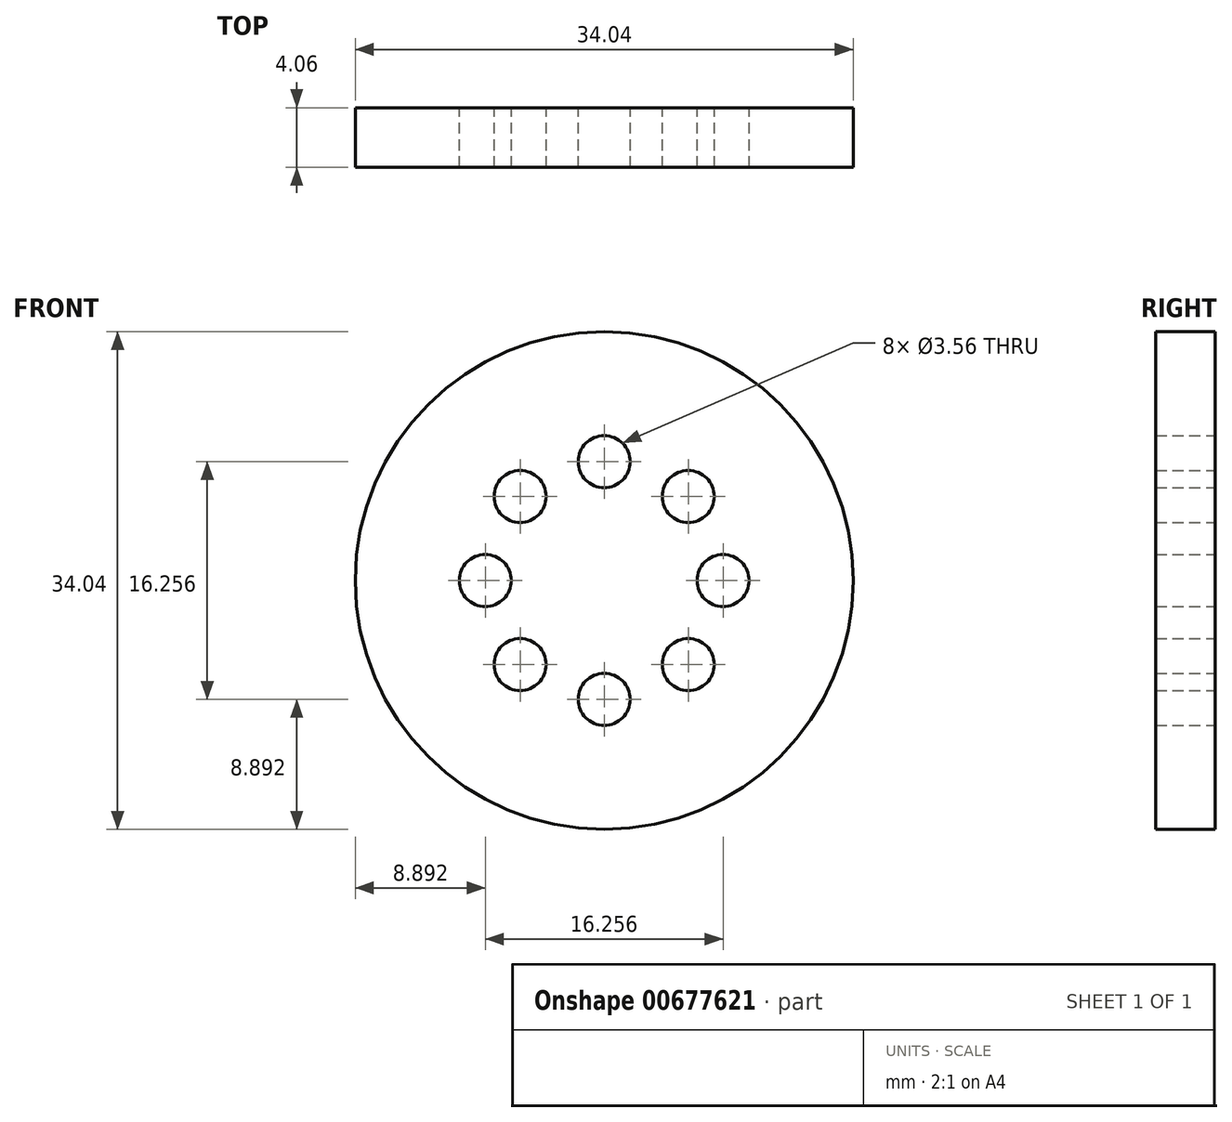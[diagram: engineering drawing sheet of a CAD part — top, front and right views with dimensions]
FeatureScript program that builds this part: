
annotation { "Feature Type Name" : "Feature", "Feature Type Description" : "" }
export const myFeature = defineFeature(function(context is Context, id is Id, definition is map)
    precondition{}
    {
        {
            var Q0;
            Q0=qCreatedBy(makeId("Front.planeOp"),FACE);
            var sketch = newSketch(context, id + "F0", { "sketchPlane" : qUnion([Q0])});
            skCircle(sketch, "E0", {"center": v(0, 0) * mm, "radius": 17.02 * mm});
            skSolve(sketch);
        }
        {
            var Q0;
            Q0=makeQuery(id+"F0.imprint","IMPRINT",FACE,{"disambiguationData":[TD([[makeQuery(id+"F0.imprint","IMPRINT",EDGE,{"derivedFrom":sQuery(id+"F0.wireOp",EDGE,"E0")}),1.0]])]});
            var sketch = newSketch(context, id + "F1", { "sketchPlane" : qUnion([Q0])});
            skCircle(sketch, "E1", {"center": v(0, -8.13) * mm, "radius": 1.78 * mm});
            skCircle(sketch, "E2.1.0", {"center": v(5.75, -5.75) * mm, "radius": 1.78 * mm});
            skCircle(sketch, "E2.2.0", {"center": v(8.13, 0) * mm, "radius": 1.78 * mm});
            skCircle(sketch, "E2.3.0", {"center": v(5.75, 5.75) * mm, "radius": 1.78 * mm});
            skCircle(sketch, "E2.4.0", {"center": v(0, 8.13) * mm, "radius": 1.78 * mm});
            skCircle(sketch, "E2.5.0", {"center": v(-5.75, 5.75) * mm, "radius": 1.78 * mm});
            skCircle(sketch, "E2.6.0", {"center": v(-8.13, 0) * mm, "radius": 1.78 * mm});
            skCircle(sketch, "E2.7.0", {"center": v(-5.75, -5.75) * mm, "radius": 1.78 * mm});
            skPoint(sketch, "E2.center", {"position": v(0, 0) * mm});
            skSolve(sketch);
        }
        {
            var Q0;
            Q0=makeQuery(id+"F0.imprint","IMPRINT",FACE,{"disambiguationData":[TD([[makeQuery(id+"F0.imprint","IMPRINT",EDGE,{"derivedFrom":sQuery(id+"F0.wireOp",EDGE,"E0")}),1.0]])]});
            extrude(context, id + "F2", {"entities" : qUnion([Q0]), "depth" : 4.06 * mm, "offsetDistance" : 25.4 * mm});
        }
        {
            var Q0;
            Q0=makeQuery(id+"F1.imprint","IMPRINT",FACE,{"disambiguationData":[TD([[makeQuery(id+"F1.imprint","IMPRINT",EDGE,{"derivedFrom":sQuery(id+"F1.wireOp",EDGE,"E2.4.0")}),1.0]])]});
            var Q1;
            Q1=makeQuery(id+"F1.imprint","IMPRINT",FACE,{"disambiguationData":[TD([[makeQuery(id+"F1.imprint","IMPRINT",EDGE,{"derivedFrom":sQuery(id+"F1.wireOp",EDGE,"E2.5.0")}),1.0]])]});
            var Q2;
            Q2=makeQuery(id+"F1.imprint","IMPRINT",FACE,{"disambiguationData":[TD([[makeQuery(id+"F1.imprint","IMPRINT",EDGE,{"derivedFrom":sQuery(id+"F1.wireOp",EDGE,"E2.6.0")}),1.0]])]});
            var Q3;
            Q3=makeQuery(id+"F1.imprint","IMPRINT",FACE,{"disambiguationData":[TD([[makeQuery(id+"F1.imprint","IMPRINT",EDGE,{"derivedFrom":sQuery(id+"F1.wireOp",EDGE,"E2.7.0")}),1.0]])]});
            var Q4;
            Q4=makeQuery(id+"F1.imprint","IMPRINT",FACE,{"disambiguationData":[TD([[makeQuery(id+"F1.imprint","IMPRINT",EDGE,{"derivedFrom":sQuery(id+"F1.wireOp",EDGE,"E1")}),1.0]])]});
            var Q5;
            Q5=makeQuery(id+"F1.imprint","IMPRINT",FACE,{"disambiguationData":[TD([[makeQuery(id+"F1.imprint","IMPRINT",EDGE,{"derivedFrom":sQuery(id+"F1.wireOp",EDGE,"E2.1.0")}),1.0]])]});
            var Q6;
            Q6=makeQuery(id+"F1.imprint","IMPRINT",FACE,{"disambiguationData":[TD([[makeQuery(id+"F1.imprint","IMPRINT",EDGE,{"derivedFrom":sQuery(id+"F1.wireOp",EDGE,"E2.2.0")}),1.0]])]});
            var Q7;
            Q7=makeQuery(id+"F1.imprint","IMPRINT",FACE,{"disambiguationData":[TD([[makeQuery(id+"F1.imprint","IMPRINT",EDGE,{"derivedFrom":sQuery(id+"F1.wireOp",EDGE,"E2.3.0")}),1.0]])]});
            extrude(context, id + "F3", {"entities" : qUnion([Q0, Q1, Q2, Q3, Q4, Q5, Q6, Q7]), "operationType" : NewBodyOperationType.REMOVE, "depth" : 25.4 * mm, "offsetDistance" : 25.4 * mm});
        }
    });
